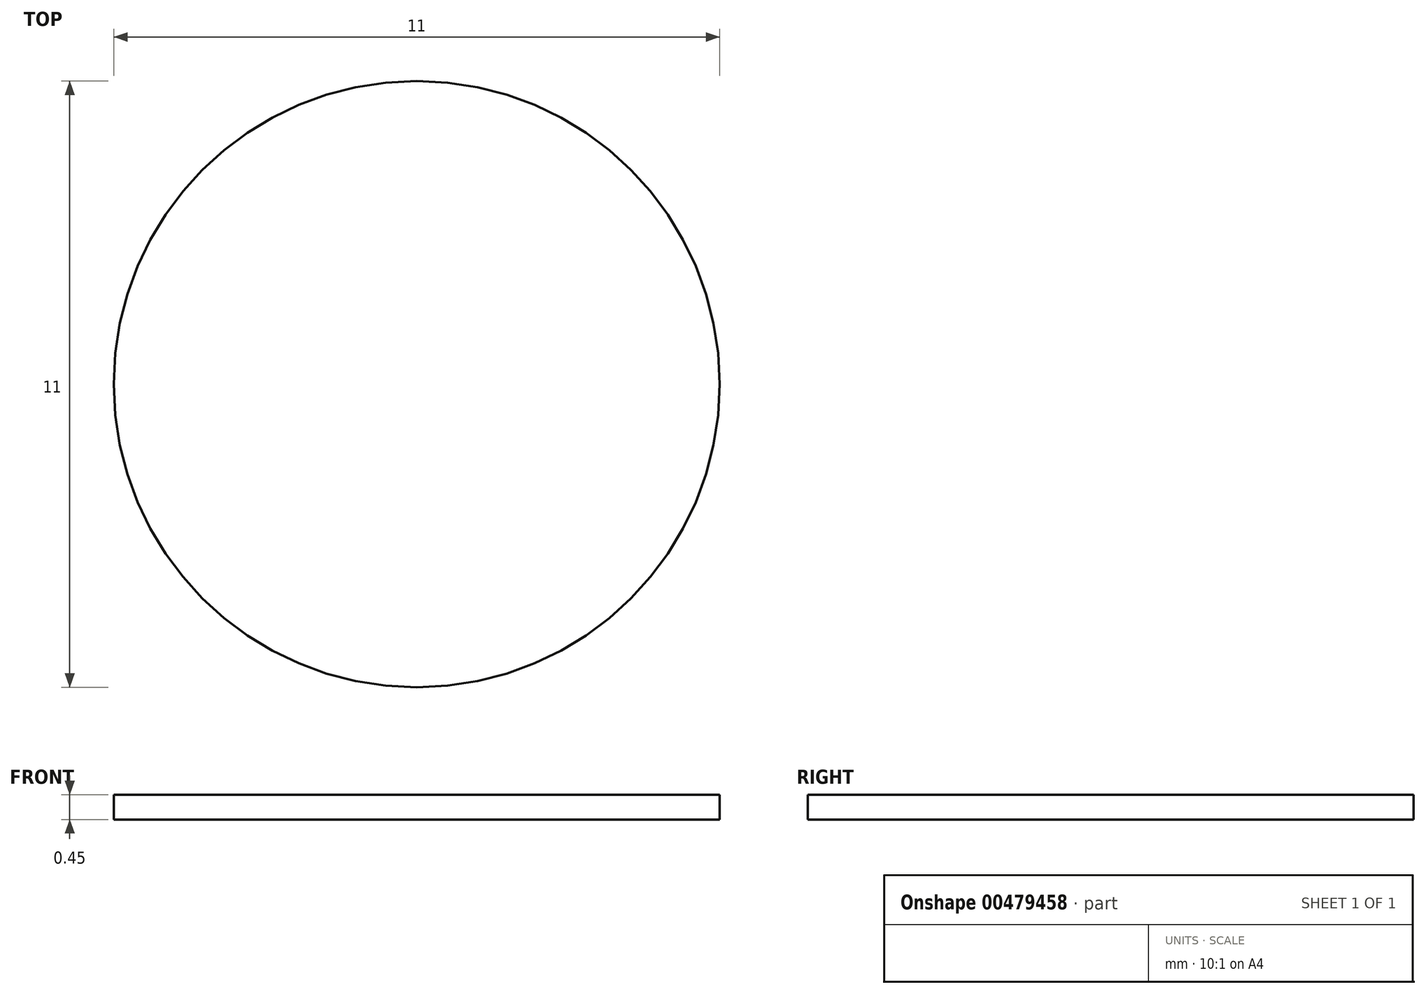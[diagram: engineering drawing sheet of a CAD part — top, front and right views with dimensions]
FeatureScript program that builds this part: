
annotation { "Feature Type Name" : "Feature", "Feature Type Description" : "" }
export const myFeature = defineFeature(function(context is Context, id is Id, definition is map)
    precondition{}
    {
        {
            var Q0;
            Q0=qCreatedBy(makeId("Top.planeOp"),FACE);
            var sketch = newSketch(context, id + "F0", { "sketchPlane" : qUnion([Q0])});
            skCircle(sketch, "E0", {"center": v(0, 0) * mm, "radius": 5.5 * mm});
            skSolve(sketch);
        }
        {
            var Q0;
            Q0=makeQuery(id+"F0.imprint","IMPRINT",FACE,{"disambiguationData":[TD([[makeQuery(id+"F0.imprint","IMPRINT",EDGE,{"derivedFrom":sQuery(id+"F0.wireOp",EDGE,"E0")}),1.0]])]});
            extrude(context, id + "F1", {"entities" : qUnion([Q0]), "depth" : 0.45 * mm});
        }
    });
